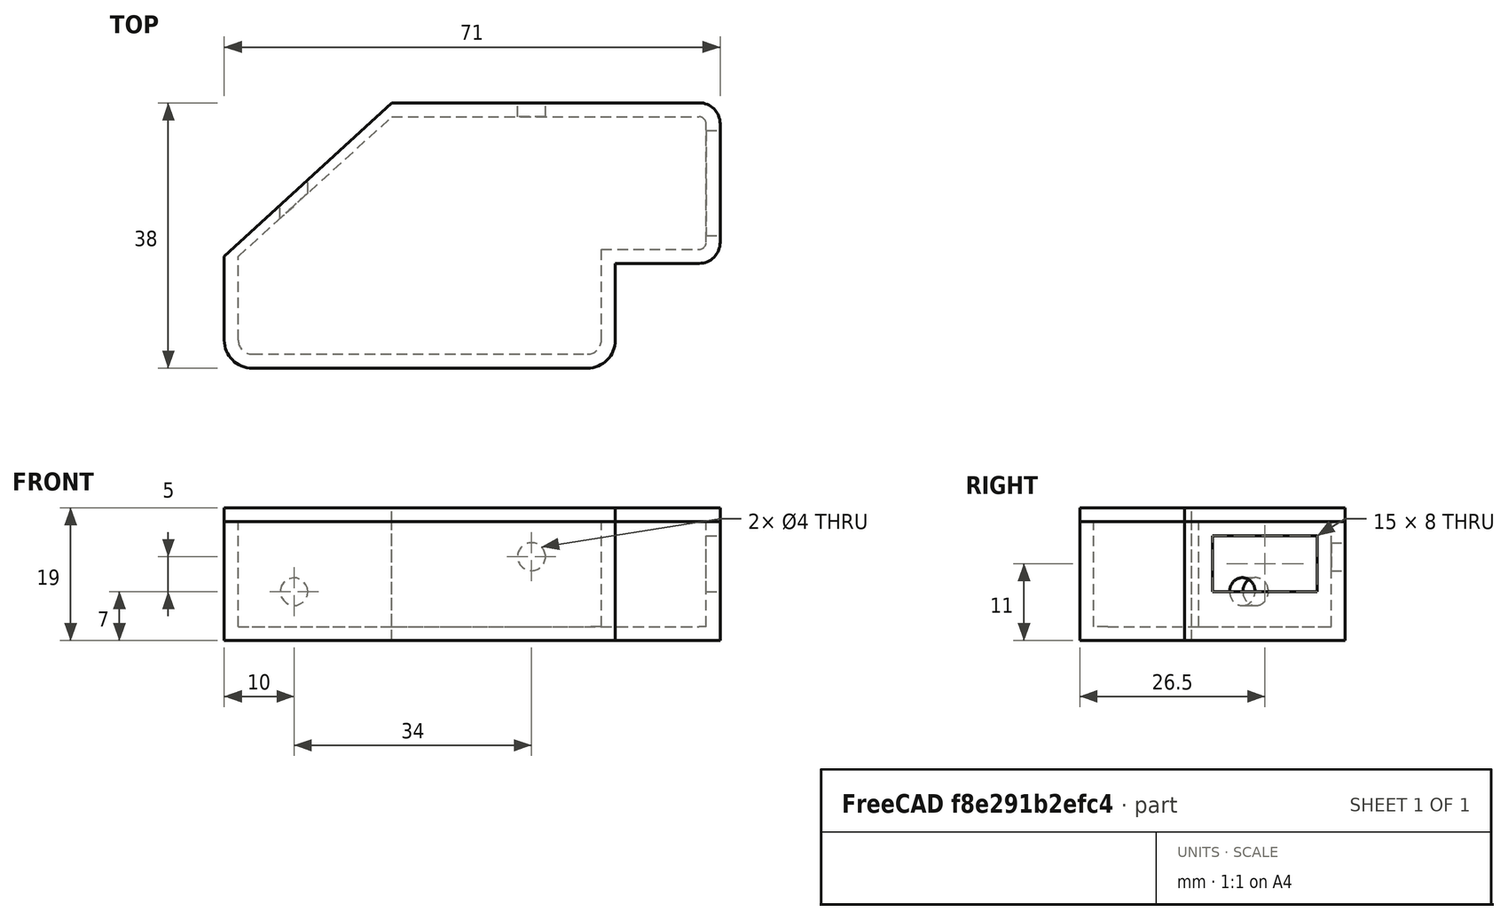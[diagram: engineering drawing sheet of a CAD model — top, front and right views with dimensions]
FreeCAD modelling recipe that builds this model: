
FCSTD DOCUMENT  (FreeCAD 0.20R29603 (Git))
Label: step-down-adapter
License: All rights reserved
LicenseURL: http://en.wikipedia.org/wiki/All_rights_reserved
objects: Part::Fillet×9, Part::Box×7, Part::Cut×7, Part::Chamfer×3, Part::Cylinder×2
note: 28 computed .brp shape members not serialized (recipe doc carries the construction recipe); baked Part::Feature solids carry a one-line shape summary decoded from their .brp

FEATURE [Part::Box] Box  label="Cube"
  AttacherType = Attacher::AttachEngine3D
  Height = 15
  Length = 67
  Width = 34
FEATURE [Part::Box] Box001  label="Cube001"
  AttacherType = Attacher::AttachEngine3D
  Height = 17
  Length = 71
  Placement = pos=(-2,-2,-2) rot=(0,0,1;0rad)
  Width = 38
FEATURE [Part::Box] Box002  label="Cube002"
  AttacherType = Attacher::AttachEngine3D
  Height = 15
  Length = 15
  Placement = pos=(52,0,0) rot=(0,0,1;0rad)
  Width = 15
FEATURE [Part::Box] Box003  label="Cube003"
  AttacherType = Attacher::AttachEngine3D
  Height = 17
  Length = 15
  Placement = pos=(54,-2,-2) rot=(0,0,1;0rad)
  Width = 15
FEATURE [Part::Cut] Cut
  Base = -> Box
  Tool = -> Box002
FEATURE [Part::Chamfer] Chamfer
  Base = -> Cut
  Edges = 1 edges: [Edge3 r1=20 r2=22]
FEATURE [Part::Cut] Cut001
  Base = -> Box001
  Tool = -> Chamfer
FEATURE [Part::Cut] Cut002
  Base = -> Cut001
  Tool = -> Box003
FEATURE [Part::Chamfer] Chamfer001
  Base = -> Cut002
  Edges = 1 edges: [Edge3 r1=22 r2=24]
FEATURE [Part::Box] Box004  label="Cube004"
  AttacherType = Attacher::AttachEngine3D
  Height = 8
  Length = 15
  Placement = pos=(66,17,5) rot=(0,0,1;0rad)
  Width = 15
FEATURE [Part::Cylinder] Cylinder
  Angle = 360
  AttacherType = Attacher::AttachEngine3D
  FirstAngle = 0
  Height = 10
  Placement = pos=(42,32,10) rot=(-1,0,0;1.5708rad)
  Radius = 2
  SecondAngle = 0
FEATURE [Part::Cut] Cut003
  Base = -> Chamfer001
  Tool = -> Box004
FEATURE [Part::Cylinder] Cylinder001
  Angle = 360
  AttacherType = Attacher::AttachEngine3D
  FirstAngle = 0
  Height = 10
  Placement = pos=(8,17,5) rot=(-1,0,0;1.5708rad)
  Radius = 2
  SecondAngle = 0
FEATURE [Part::Cut] Cut004
  Base = -> Cut003
  Tool = -> Cylinder
FEATURE [Part::Cut] Cut005
  Base = -> Cut004
  Tool = -> Cylinder001
FEATURE [Part::Fillet] Fillet
  Base = -> Cut005
  Edges = 1 edges r=4: [Edge2]
FEATURE [Part::Fillet] Fillet001
  Base = -> Fillet
  Edges = 1 edges r=2: [Edge38]
FEATURE [Part::Fillet] Fillet002
  Base = -> Fillet001
  Edges = 1 edges r=4: [Edge45]
FEATURE [Part::Fillet] Fillet003
  Base = -> Fillet002
  Edges = 1 edges r=2: [Edge59]
FEATURE [Part::Fillet] Fillet004
  Base = -> Fillet003
  Edges = 2 edges r=1: [Edge25,Edge29]
FEATURE [Part::Fillet] Fillet005  label="Bottom"
  Base = -> Fillet004
  Edges = 2 edges r=3: [Edge57,Edge59]
FEATURE [Part::Box] Box005  label="Cube005"
  AttacherType = Attacher::AttachEngine3D
  Height = 2
  Length = 71
  Placement = pos=(-2,-2,0) rot=(0,0,1;0rad)
  Width = 38
FEATURE [Part::Box] Box006  label="Cube006"
  AttacherType = Attacher::AttachEngine3D
  Height = 2
  Length = 15
  Placement = pos=(54,-2,0) rot=(0,0,1;0rad)
  Width = 15
FEATURE [Part::Cut] Cut006
  Base = -> Box005
  Tool = -> Box006
FEATURE [Part::Fillet] Fillet006
  Base = -> Cut006
  Edges = 1 edges r=4: [Edge6]
FEATURE [Part::Fillet] Fillet007
  Base = -> Fillet006
  Edges = 1 edges r=4: [Edge2]
FEATURE [Part::Chamfer] Chamfer002
  Base = -> Fillet007
  Edges = 1 edges: [Edge21 r1=22 r2=24]
FEATURE [Part::Fillet] Fillet008  label="Top"
  Base = -> Chamfer002
  Edges = 2 edges r=3: [Edge18,Edge21]
  Placement = pos=(0,0,15) rot=(0,0,1;0rad)
